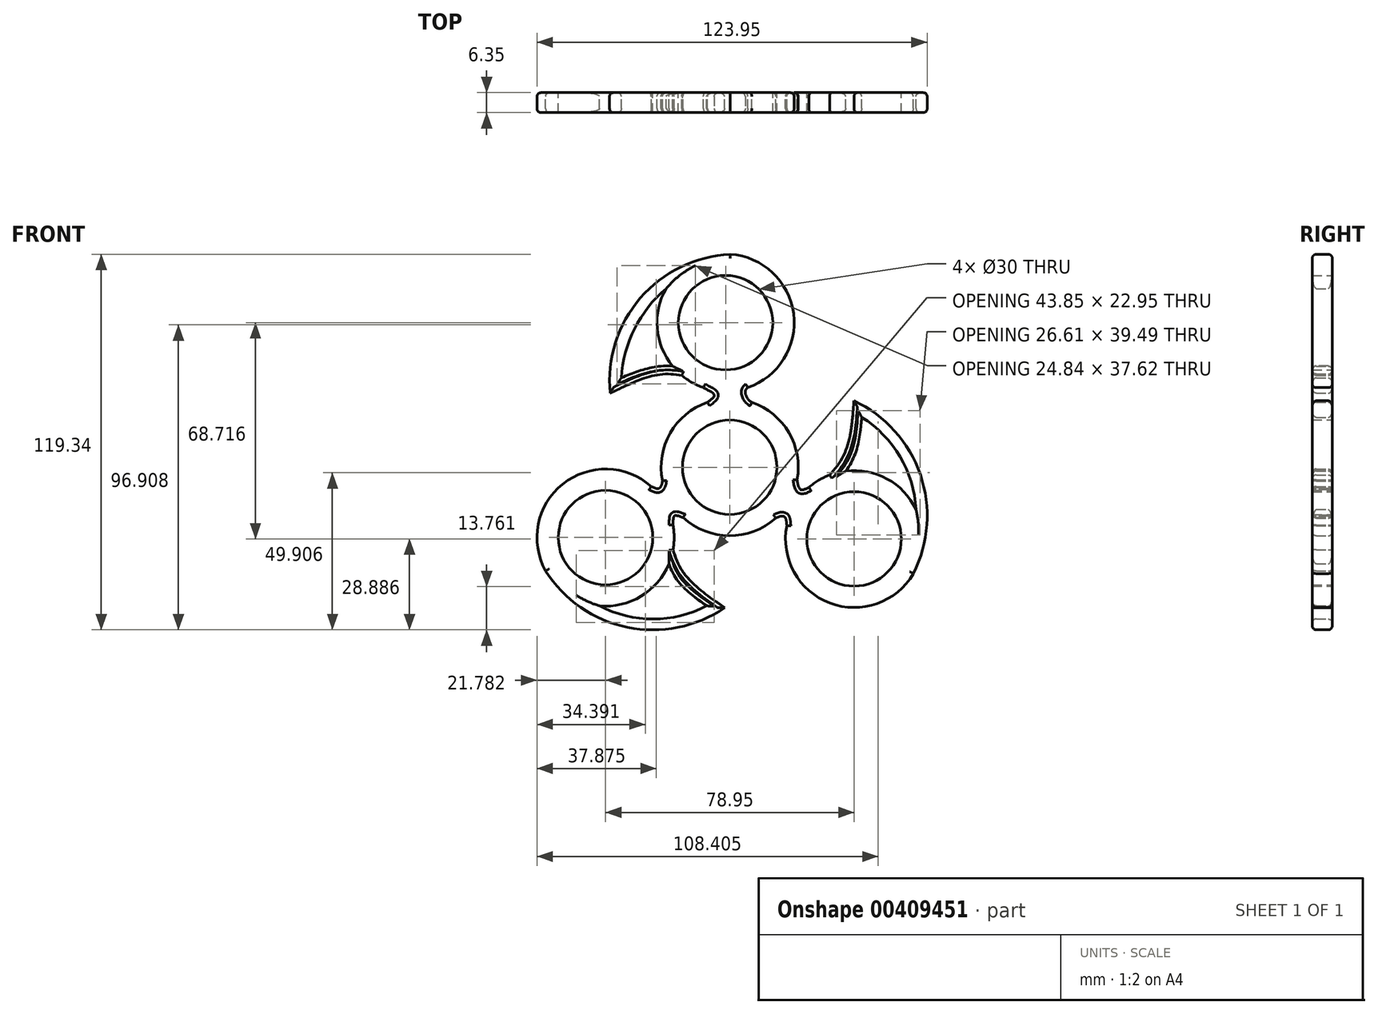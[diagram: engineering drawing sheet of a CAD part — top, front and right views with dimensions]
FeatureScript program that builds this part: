
annotation { "Feature Type Name" : "Feature", "Feature Type Description" : "" }
export const myFeature = defineFeature(function(context is Context, id is Id, definition is map)
    precondition{}
    {
        {
            var Q0;
            Q0=qCreatedBy(makeId("Front.planeOp"),FACE);
            var sketch = newSketch(context, id + "F0", { "sketchPlane" : qUnion([Q0])});
            skCircle(sketch, "E0", {"center": v(-0.12, 1.03) * mm, "radius": 21.78 * mm});
            skCircle(sketch, "E1", {"center": v(-1.41, 46.96) * mm, "radius": 21.78 * mm});
            skFitSpline(sketch, "E2", {"points": [v(-38.1, 24.56) * mm, v(-20.56, 30.63) * mm, v(0, 25.23) * mm], "startDerivative": vector(35.7, 16.53) * mm, "endDerivative": vector(40.81, -14.8) * mm});
            skArc(sketch, "E3", {"start": v(0, 68.7) * mm, "mid": v(-28.49, 54.77) * mm, "end": v(-38.1, 24.56) * mm});
            skLineSegment(sketch, "E4", {"start": v(0, 25.23) * mm, "end": v(0, 22.8) * mm});
            skPoint(sketch, "E5.endSnap0", {"position": v(0, 24.02) * mm});
            skLineSegment(sketch, "E6", {"start": v(0, 25.23) * mm, "end": v(0, 26.39) * mm});
            skLineSegment(sketch, "E7", {"start": v(0, 22.8) * mm, "end": v(0, 21.65) * mm});
            skFitSpline(sketch, "E8", {"points": [v(5.6, 26.34) * mm, v(5.03, 24.02) * mm, v(6.9, 21.65) * mm], "startDerivative": vector(-6.67, -4.9) * mm, "endDerivative": vector(7.44, -4.58) * mm});
            skFitSpline(sketch, "E9", {"points": [v(-7.14, 21.65) * mm, v(-5.03, 24.02) * mm, v(-8.43, 26.34) * mm], "startDerivative": vector(6.1, 4.9) * mm, "endDerivative": vector(-6.85, 4.59) * mm});
            skLineSegment(sketch, "E10", {"start": v(-0.12, 1.03) * mm, "end": v(-0.12, 22.8) * mm});
            skLineSegment(sketch, "E11", {"start": v(-0.12, 1.03) * mm, "end": v(-19.05, -9.75) * mm});
            skLineSegment(sketch, "E12", {"start": v(-0.12, 1.03) * mm, "end": v(18.7, -9.95) * mm});
            skCircle(sketch, "E13", {"center": v(39.4, -21.75) * mm, "radius": 21.78 * mm});
            skFitSpline(sketch, "E14", {"points": [v(39.36, 22.14) * mm, v(35.74, 4.14) * mm, v(20.48, -10.97) * mm], "startDerivative": vector(-3.53, -39.18) * mm, "endDerivative": vector(-33.88, -27.18) * mm});
            skArc(sketch, "E15", {"start": v(58.2, -32.75) * mm, "mid": v(60.43, -1.3) * mm, "end": v(39.36, 22.14) * mm});
            skPoint(sketch, "E16.endSnap0", {"position": v(19.87, -10.4) * mm});
            skLineSegment(sketch, "E17", {"start": v(20.48, -10.97) * mm, "end": v(21.49, -11.55) * mm});
            skFitSpline(sketch, "E18", {"points": [v(18.04, -17.52) * mm, v(17.36, -14.75) * mm, v(14.36, -15.19) * mm], "startDerivative": vector(-0.91, 8.23) * mm, "endDerivative": vector(-7.69, -4.15) * mm});
            skFitSpline(sketch, "E19", {"points": [v(21.3, -2.98) * mm, v(22.39, -6.03) * mm, v(25.05, -5.37) * mm], "startDerivative": vector(1.2, -7.73) * mm, "endDerivative": vector(7.4, 3.64) * mm});
            skCircle(sketch, "E20", {"center": v(-39.55, -21.3) * mm, "radius": 21.78 * mm});
            skFitSpline(sketch, "E21", {"points": [v(-1.73, -43.6) * mm, v(-15.67, -31.1) * mm, v(-20.64, -10.5) * mm], "startDerivative": vector(-31.94, 22.96) * mm, "endDerivative": vector(-6.17, 43) * mm});
            skArc(sketch, "E22", {"start": v(-58.58, -31.9) * mm, "mid": v(-32.63, -49.82) * mm, "end": v(-1.73, -43.6) * mm});
            skPoint(sketch, "E23.endSnap0", {"position": v(-20.11, -10.05) * mm});
            skLineSegment(sketch, "E24", {"start": v(-20.64, -10.5) * mm, "end": v(-21.65, -11.07) * mm});
            skFitSpline(sketch, "E25", {"points": [v(-25.04, -5.06) * mm, v(-22.58, -5.66) * mm, v(-21.44, -2.86) * mm], "startDerivative": vector(7.55, -3.4) * mm, "endDerivative": vector(0.34, 8.73) * mm});
            skFitSpline(sketch, "E26", {"points": [v(-14.53, -15.1) * mm, v(-17.64, -14.43) * mm, v(-18.14, -17.29) * mm], "startDerivative": vector(-7.27, 2.9) * mm, "endDerivative": vector(-0.63, -8.22) * mm});
            skLineSegment(sketch, "E27.0", {"start": v(-20.11, -10.05) * mm, "end": v(-22.58, -5.66) * mm});
            skLineSegment(sketch, "E28", {"start": v(19.87, -10.4) * mm, "end": v(17.36, -14.75) * mm});
            skArc(sketch, "E29", {"start": v(5.47, 67.33) * mm, "mid": v(-23.16, 55.15) * mm, "end": v(-34.6, 26.22) * mm});
            skArc(sketch, "E30", {"start": v(56.42, -28.1) * mm, "mid": v(56.8, -1.44) * mm, "end": v(39.05, 18.47) * mm});
            skArc(sketch, "E31", {"start": v(-53.44, -33.03) * mm, "mid": v(-30.72, -46.65) * mm, "end": v(-4.74, -41.46) * mm});
            skFitSpline(sketch, "E32", {"points": [v(-4.12, -45.3) * mm, v(-18.06, -32.8) * mm, v(-22.02, -11.5) * mm], "startDerivative": vector(-31.94, 22.96) * mm, "endDerivative": vector(-6.17, 43) * mm});
            skFitSpline(sketch, "E33", {"points": [v(42.14, 20.6) * mm, v(38.52, 2.6) * mm, v(23.26, -12.5) * mm], "startDerivative": vector(-3.53, -39.18) * mm, "endDerivative": vector(-33.88, -27.18) * mm});
            skFitSpline(sketch, "E34", {"points": [v(-38.28, 27.73) * mm, v(-20.71, 33.2) * mm, v(-0.22, 28.08) * mm], "startDerivative": vector(35.7, 16.53) * mm, "endDerivative": vector(40.12, -16.68) * mm});
            skSolve(sketch);
        }
        {
            var Q0;
            {var subQ1=sQuery(id+"F0.wireOp",EDGE,"E1");var subQ4=sQuery(id+"F0.wireOp",EDGE,"E3");var subQ7=makeQuery(id+"F0.imprint","INTERSECT",VERTEX,{"disambiguationData":[OD(1.0)],"derivedFrom":[subQ1,subQ4]});Q0=makeQuery(id+"F0.imprint","IMPRINT",FACE,{"disambiguationData":[TD([[makeQuery(id+"F0.imprint","IMPRINT",EDGE,{"disambiguationData":[TD([[subQ7,-1.0]])],"derivedFrom":subQ1}),1.0]])]});}
            var Q1;
            {var subQ0=sQuery(id+"F0.wireOp",EDGE,"E11");Q1=makeQuery(id+"F0.imprint","IMPRINT",FACE,{"disambiguationData":[TD([[makeQuery(id+"F0.imprint","IMPRINT",EDGE,{"derivedFrom":subQ0}),-1.0]])]});}
            var Q2;
            {var subQ0=sQuery(id+"F0.wireOp",EDGE,"E11");Q2=makeQuery(id+"F0.imprint","IMPRINT",FACE,{"disambiguationData":[TD([[makeQuery(id+"F0.imprint","IMPRINT",EDGE,{"derivedFrom":subQ0}),1.0]])]});}
            var Q3;
            {var subQ1=sQuery(id+"F0.wireOp",EDGE,"E20");var subQ4=sQuery(id+"F0.wireOp",EDGE,"E22");var subQ7=makeQuery(id+"F0.imprint","INTERSECT",VERTEX,{"disambiguationData":[OD(1.0)],"derivedFrom":[subQ1,subQ4]});Q3=makeQuery(id+"F0.imprint","IMPRINT",FACE,{"disambiguationData":[TD([[makeQuery(id+"F0.imprint","IMPRINT",EDGE,{"disambiguationData":[TD([[subQ7,-1.0]])],"derivedFrom":subQ1}),1.0]])]});}
            var Q4;
            {var subQ0=sQuery(id+"F0.wireOp",EDGE,"E22");var subQ1=sQuery(id+"F0.wireOp",EDGE,"E20");var subQ2=makeQuery(id+"F0.imprint","INTERSECT",VERTEX,{"disambiguationData":[OD(1.0)],"derivedFrom":[subQ1,subQ0]});Q4=makeQuery(id+"F0.imprint","IMPRINT",FACE,{"disambiguationData":[TD([[makeQuery(id+"F0.imprint","IMPRINT",EDGE,{"disambiguationData":[TD([[subQ2,-1.0]])],"derivedFrom":subQ1}),-1.0]])]});}
            var Q5;
            {var subQ1=sQuery(id+"F0.wireOp",EDGE,"E13");var subQ6=makeQuery(id+"F0.imprint","IMPRINT",VERTEX,{"disambiguationData":[OD(0.0)],"derivedFrom":subQ1});Q5=makeQuery(id+"F0.imprint","IMPRINT",FACE,{"disambiguationData":[TD([[makeQuery(id+"F0.imprint","IMPRINT",EDGE,{"disambiguationData":[TD([[subQ6,1.0]])],"derivedFrom":subQ1}),1.0]])]});}
            var Q6;
            {var subQ0=sQuery(id+"F0.wireOp",EDGE,"E15");var subQ1=sQuery(id+"F0.wireOp",EDGE,"E13");var subQ2=makeQuery(id+"F0.imprint","INTERSECT",VERTEX,{"disambiguationData":[OD(1.0)],"derivedFrom":[subQ1,subQ0]});Q6=makeQuery(id+"F0.imprint","IMPRINT",FACE,{"disambiguationData":[TD([[makeQuery(id+"F0.imprint","IMPRINT",EDGE,{"disambiguationData":[TD([[subQ2,-1.0]])],"derivedFrom":subQ1}),-1.0]])]});}
            var Q7;
            {var subQ0=sQuery(id+"F0.wireOp",EDGE,"E20");var subQ1=makeQuery(id+"F0.imprint","INTERSECT",VERTEX,{"derivedFrom":[subQ0,sQuery(id+"F0.wireOp",EDGE,"E26")]});Q7=makeQuery(id+"F0.imprint","IMPRINT",FACE,{"disambiguationData":[TD([[makeQuery(id+"F0.imprint","IMPRINT",EDGE,{"disambiguationData":[TD([[subQ1,1.0]])],"derivedFrom":subQ0}),1.0]])]});}
            var Q8;
            {var subQ4=sQuery(id+"F0.wireOp",EDGE,"E0");var subQ5=makeQuery(id+"F0.imprint","INTERSECT",VERTEX,{"derivedFrom":[subQ4,sQuery(id+"F0.wireOp",EDGE,"E11")]});Q8=makeQuery(id+"F0.imprint","IMPRINT",FACE,{"disambiguationData":[TD([[makeQuery(id+"F0.imprint","IMPRINT",EDGE,{"disambiguationData":[TD([[subQ5,1.0]])],"derivedFrom":subQ4}),-1.0]])]});}
            var Q9;
            {var subQ0=sQuery(id+"F0.wireOp",EDGE,"E1");var subQ1=makeQuery(id+"F0.imprint","INTERSECT",VERTEX,{"derivedFrom":[subQ0,sQuery(id+"F0.wireOp",EDGE,"E9")]});Q9=makeQuery(id+"F0.imprint","IMPRINT",FACE,{"disambiguationData":[TD([[makeQuery(id+"F0.imprint","IMPRINT",EDGE,{"disambiguationData":[TD([[subQ1,1.0]])],"derivedFrom":subQ0}),1.0]])]});}
            var Q10;
            {var subQ0=sQuery(id+"F0.wireOp",EDGE,"E4");Q10=makeQuery(id+"F0.imprint","IMPRINT",FACE,{"disambiguationData":[TD([[makeQuery(id+"F0.imprint","IMPRINT",EDGE,{"derivedFrom":subQ0}),-1.0]])]});}
            var Q11;
            {var subQ0=sQuery(id+"F0.wireOp",EDGE,"E4");Q11=makeQuery(id+"F0.imprint","IMPRINT",FACE,{"disambiguationData":[TD([[makeQuery(id+"F0.imprint","IMPRINT",EDGE,{"derivedFrom":subQ0}),1.0]])]});}
            var Q12;
            {var subQ0=sQuery(id+"F0.wireOp",EDGE,"E13");var subQ1=makeQuery(id+"F0.imprint","IMPRINT",VERTEX,{"disambiguationData":[OD(1.0)],"derivedFrom":subQ0});Q12=makeQuery(id+"F0.imprint","IMPRINT",FACE,{"disambiguationData":[TD([[makeQuery(id+"F0.imprint","IMPRINT",EDGE,{"disambiguationData":[TD([[subQ1,1.0]])],"derivedFrom":subQ0}),1.0]])]});}
            var Q13;
            {var subQ7=sQuery(id+"F0.wireOp",EDGE,"E19");Q13=makeQuery(id+"F0.imprint","IMPRINT",FACE,{"disambiguationData":[TD([[makeQuery(id+"F0.imprint","IMPRINT",EDGE,{"derivedFrom":subQ7}),-1.0]])]});}
            var Q14;
            {var subQ1=sQuery(id+"F0.wireOp",EDGE,"E13");var subQ4=sQuery(id+"F0.wireOp",EDGE,"E15");var subQ7=makeQuery(id+"F0.imprint","INTERSECT",VERTEX,{"disambiguationData":[OD(1.0)],"derivedFrom":[subQ1,subQ4]});Q14=makeQuery(id+"F0.imprint","IMPRINT",FACE,{"disambiguationData":[TD([[makeQuery(id+"F0.imprint","IMPRINT",EDGE,{"disambiguationData":[TD([[subQ7,-1.0]])],"derivedFrom":subQ1}),1.0]])]});}
            var Q15;
            {var subQ0=sQuery(id+"F0.wireOp",EDGE,"E13");var subQ1=makeQuery(id+"F0.imprint","INTERSECT",VERTEX,{"derivedFrom":[subQ0,sQuery(id+"F0.wireOp",EDGE,"E19")]});Q15=makeQuery(id+"F0.imprint","IMPRINT",FACE,{"disambiguationData":[TD([[makeQuery(id+"F0.imprint","IMPRINT",EDGE,{"disambiguationData":[TD([[subQ1,1.0]])],"derivedFrom":subQ0}),1.0]])]});}
            var Q16;
            {var subQ0=sQuery(id+"F0.wireOp",EDGE,"E33");var subQ1=sQuery(id+"F0.wireOp",EDGE,"E13");var subQ2=makeQuery(id+"F0.imprint","INTERSECT",VERTEX,{"derivedFrom":[subQ1,subQ0]});Q16=makeQuery(id+"F0.imprint","IMPRINT",FACE,{"disambiguationData":[TD([[makeQuery(id+"F0.imprint","IMPRINT",EDGE,{"disambiguationData":[TD([[subQ2,-1.0]])],"derivedFrom":subQ1}),-1.0]])]});}
            var Q17;
            {var subQ0=sQuery(id+"F0.wireOp",EDGE,"E32");var subQ1=sQuery(id+"F0.wireOp",EDGE,"E20");var subQ2=makeQuery(id+"F0.imprint","INTERSECT",VERTEX,{"derivedFrom":[subQ1,subQ0]});Q17=makeQuery(id+"F0.imprint","IMPRINT",FACE,{"disambiguationData":[TD([[makeQuery(id+"F0.imprint","IMPRINT",EDGE,{"disambiguationData":[TD([[subQ2,-1.0]])],"derivedFrom":subQ1}),-1.0]])]});}
            var Q18;
            {var subQ0=sQuery(id+"F0.wireOp",EDGE,"E22");var subQ1=sQuery(id+"F0.wireOp",EDGE,"E21");var subQ2=makeQuery(id+"F0.imprint","INTERSECT",VERTEX,{"derivedFrom":[subQ1,subQ0]});Q18=makeQuery(id+"F0.imprint","IMPRINT",FACE,{"disambiguationData":[TD([[makeQuery(id+"F0.imprint","IMPRINT",EDGE,{"disambiguationData":[TD([[subQ2,-1.0]])],"derivedFrom":subQ1}),1.0]])]});}
            var Q19;
            {var subQ0=sQuery(id+"F0.wireOp",EDGE,"E3");var subQ1=sQuery(id+"F0.wireOp",EDGE,"E1");var subQ2=makeQuery(id+"F0.imprint","INTERSECT",VERTEX,{"disambiguationData":[OD(1.0)],"derivedFrom":[subQ1,subQ0]});Q19=makeQuery(id+"F0.imprint","IMPRINT",FACE,{"disambiguationData":[TD([[makeQuery(id+"F0.imprint","IMPRINT",EDGE,{"disambiguationData":[TD([[subQ2,-1.0]])],"derivedFrom":subQ1}),-1.0]])]});}
            var Q20;
            {var subQ0=sQuery(id+"F0.wireOp",EDGE,"E34");var subQ1=sQuery(id+"F0.wireOp",EDGE,"E1");var subQ2=makeQuery(id+"F0.imprint","INTERSECT",VERTEX,{"derivedFrom":[subQ1,subQ0]});Q20=makeQuery(id+"F0.imprint","IMPRINT",FACE,{"disambiguationData":[TD([[makeQuery(id+"F0.imprint","IMPRINT",EDGE,{"disambiguationData":[TD([[subQ2,-1.0]])],"derivedFrom":subQ1}),-1.0]])]});}
            var Q21;
            {var subQ0=sQuery(id+"F0.wireOp",EDGE,"E3");var subQ1=sQuery(id+"F0.wireOp",EDGE,"E2");var subQ2=makeQuery(id+"F0.imprint","INTERSECT",VERTEX,{"derivedFrom":[subQ1,subQ0]});Q21=makeQuery(id+"F0.imprint","IMPRINT",FACE,{"disambiguationData":[TD([[makeQuery(id+"F0.imprint","IMPRINT",EDGE,{"disambiguationData":[TD([[subQ2,-1.0]])],"derivedFrom":subQ1}),1.0]])]});}
            extrude(context, id + "F1", {"entities" : qUnion([Q0, Q1, Q2, Q3, Q4, Q5, Q6, Q7, Q8, Q9, Q10, Q11, Q12, Q13, Q14, Q15, Q16, Q17, Q18, Q19, Q20, Q21]), "depth" : 6.35 * mm});
        }
        {
            var Q0;
            Q0=makeQuery(id+"F1.opExtrude","CAP_EDGE",EDGE,{"disambiguationData":[OSD([sQuery(id+"F0.wireOp",EDGE,"E3")])],"isStart":false});
            var Q1;
            Q1=makeQuery(id+"F1.opExtrude","CAP_EDGE",EDGE,{"disambiguationData":[OSD([sQuery(id+"F0.wireOp",EDGE,"E2")])],"isStart":false});
            var Q2;
            Q2=makeQuery(id+"F1.opExtrude","CAP_FACE",FACE,{"disambiguationData":[OSD([sQuery(id+"F0.wireOp",EDGE,"E0"),sQuery(id+"F0.wireOp",EDGE,"E1"),sQuery(id+"F0.wireOp",EDGE,"E2"),sQuery(id+"F0.wireOp",EDGE,"E3"),sQuery(id+"F0.wireOp",EDGE,"E8"),sQuery(id+"F0.wireOp",EDGE,"E9"),sQuery(id+"F0.wireOp",EDGE,"E13"),sQuery(id+"F0.wireOp",EDGE,"E14"),sQuery(id+"F0.wireOp",EDGE,"E15"),sQuery(id+"F0.wireOp",EDGE,"E18"),sQuery(id+"F0.wireOp",EDGE,"E19"),sQuery(id+"F0.wireOp",EDGE,"E20"),sQuery(id+"F0.wireOp",EDGE,"E21"),sQuery(id+"F0.wireOp",EDGE,"E22"),sQuery(id+"F0.wireOp",EDGE,"E25"),sQuery(id+"F0.wireOp",EDGE,"E26")])],"isStart":false});
            var Q3;
            {var subQ0=sQuery(id+"F0.wireOp",EDGE,"E20");Q3=makeQuery(id+"F1.opExtrude","CAP_EDGE",EDGE,{"disambiguationData":[OSD([subQ0]),TDD([makeQuery(id+"F0.imprint","IMPRINT",EDGE,{"disambiguationData":[TD([[makeQuery(id+"F0.imprint","INTERSECT",VERTEX,{"disambiguationData":[OD(0.0)],"derivedFrom":[subQ0,sQuery(id+"F0.wireOp",EDGE,"E22")]}),1.0]])],"derivedFrom":subQ0})])],"isStart":true});}
            var Q4;
            Q4=makeQuery(id+"F1.opExtrude","CAP_EDGE",EDGE,{"disambiguationData":[OSD([sQuery(id+"F0.wireOp",EDGE,"E21")])],"isStart":true});
            var Q5;
            Q5=makeQuery(id+"F1.opExtrude","CAP_EDGE",EDGE,{"disambiguationData":[OSD([sQuery(id+"F0.wireOp",EDGE,"E22")])],"isStart":true});
            var Q6;
            {var subQ0=sQuery(id+"F0.wireOp",EDGE,"E0");Q6=makeQuery(id+"F1.opExtrude","CAP_EDGE",EDGE,{"disambiguationData":[OSD([subQ0]),TDD([makeQuery(id+"F0.imprint","IMPRINT",EDGE,{"disambiguationData":[TD([[makeQuery(id+"F0.imprint","INTERSECT",VERTEX,{"derivedFrom":[subQ0,sQuery(id+"F0.wireOp",EDGE,"E9")]}),-1.0]])],"derivedFrom":subQ0})])],"isStart":true});}
            var Q7;
            Q7=makeQuery(id+"F1.opExtrude","CAP_EDGE",EDGE,{"disambiguationData":[OSD([sQuery(id+"F0.wireOp",EDGE,"E25")])],"isStart":true});
            var Q8;
            Q8=makeQuery(id+"F1.opExtrude","CAP_FACE",FACE,{"disambiguationData":[OSD([sQuery(id+"F0.wireOp",EDGE,"E0"),sQuery(id+"F0.wireOp",EDGE,"E1"),sQuery(id+"F0.wireOp",EDGE,"E2"),sQuery(id+"F0.wireOp",EDGE,"E3"),sQuery(id+"F0.wireOp",EDGE,"E8"),sQuery(id+"F0.wireOp",EDGE,"E9"),sQuery(id+"F0.wireOp",EDGE,"E13"),sQuery(id+"F0.wireOp",EDGE,"E14"),sQuery(id+"F0.wireOp",EDGE,"E15"),sQuery(id+"F0.wireOp",EDGE,"E18"),sQuery(id+"F0.wireOp",EDGE,"E19"),sQuery(id+"F0.wireOp",EDGE,"E20"),sQuery(id+"F0.wireOp",EDGE,"E21"),sQuery(id+"F0.wireOp",EDGE,"E22"),sQuery(id+"F0.wireOp",EDGE,"E25"),sQuery(id+"F0.wireOp",EDGE,"E26")])],"isStart":true});
            fillet(context, id + "F2", {"entities" : qUnion([Q0, Q1, Q2, Q3, Q4, Q5, Q6, Q7, Q8]), "radius" : 1.27 * mm, "tangentPropagation" : true, "allowEdgeOverflow" : false});
        }
        {
            var Q0;
            Q0=sQuery(id+"F0.wireOp",VERTEX,"E34.startDerivative");
            var Q1;
            Q1=sQuery(id+"F0.wireOp",VERTEX,"E1.center");
            var Q2;
            Q2=sQuery(id+"F0.wireOp",VERTEX,"E20.center");
            var Q3;
            Q3=sQuery(id+"F0.wireOp",VERTEX,"E13.center");
            var Q4;
            Q4=sQuery(id+"F0.wireOp",VERTEX,"E12.start");
            var Q5;
            Q5=makeQuery(id+"F1.opExtrude","SWEPT_BODY",BODY,{"disambiguationData":[OSD([sQuery(id+"F0.wireOp",EDGE,"E0"),sQuery(id+"F0.wireOp",EDGE,"E1"),sQuery(id+"F0.wireOp",EDGE,"E2"),sQuery(id+"F0.wireOp",EDGE,"E3"),sQuery(id+"F0.wireOp",EDGE,"E8"),sQuery(id+"F0.wireOp",EDGE,"E9"),sQuery(id+"F0.wireOp",EDGE,"E13"),sQuery(id+"F0.wireOp",EDGE,"E14"),sQuery(id+"F0.wireOp",EDGE,"E15"),sQuery(id+"F0.wireOp",EDGE,"E18"),sQuery(id+"F0.wireOp",EDGE,"E19"),sQuery(id+"F0.wireOp",EDGE,"E20"),sQuery(id+"F0.wireOp",EDGE,"E21"),sQuery(id+"F0.wireOp",EDGE,"E22"),sQuery(id+"F0.wireOp",EDGE,"E25"),sQuery(id+"F0.wireOp",EDGE,"E26"),sQuery(id+"F0.wireOp",EDGE,"E29"),sQuery(id+"F0.wireOp",EDGE,"E30"),sQuery(id+"F0.wireOp",EDGE,"E31"),sQuery(id+"F0.wireOp",EDGE,"E32"),sQuery(id+"F0.wireOp",EDGE,"E33"),sQuery(id+"F0.wireOp",EDGE,"E34")])]});
            hole(context, id + "F3", {"style" : HoleStyle.SIMPLE, "endStyle" : HoleEndStyle.THROUGH, "oppositeDirection" : true, "holeDiameter" : 30 * mm, "isTappedThrough" : true, "tappedDepth" : 12.7 * mm, "tapClearance" : 3, "locations" : qUnion([Q0, Q1, Q2, Q3, Q4]), "scope" : qUnion([Q5])});
        }
    });
